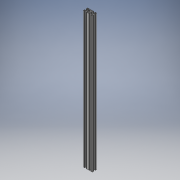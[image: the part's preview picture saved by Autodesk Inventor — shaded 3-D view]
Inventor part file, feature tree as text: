
AUTODESK INVENTOR PART (.ipt)
format: ipt  version: 2018 (Build 220112000, 112)  size: 577,024 bytes
history: native  units: mm
features: other x1, extrude x1, sketch x1
ambient origin geometry x8: Origin, YZ Plane, XZ Plane, XY Plane, X Axis, Y Axis, Z Axis, Center Point
bodies: Body1 (feature_tree)
feature tree (3):
  other  "Sólido1"
  extrude  "Extrusão1"  [1 undecoded]
  sketch  "Esboço1"  dims[d0=900.0mm d1=0.0mm]
note: 1 required parameter value undecoded (feature->parameter linkage not recoverable at this tier; creation-order binding heuristic only, values carry confidence <= 0.55)
